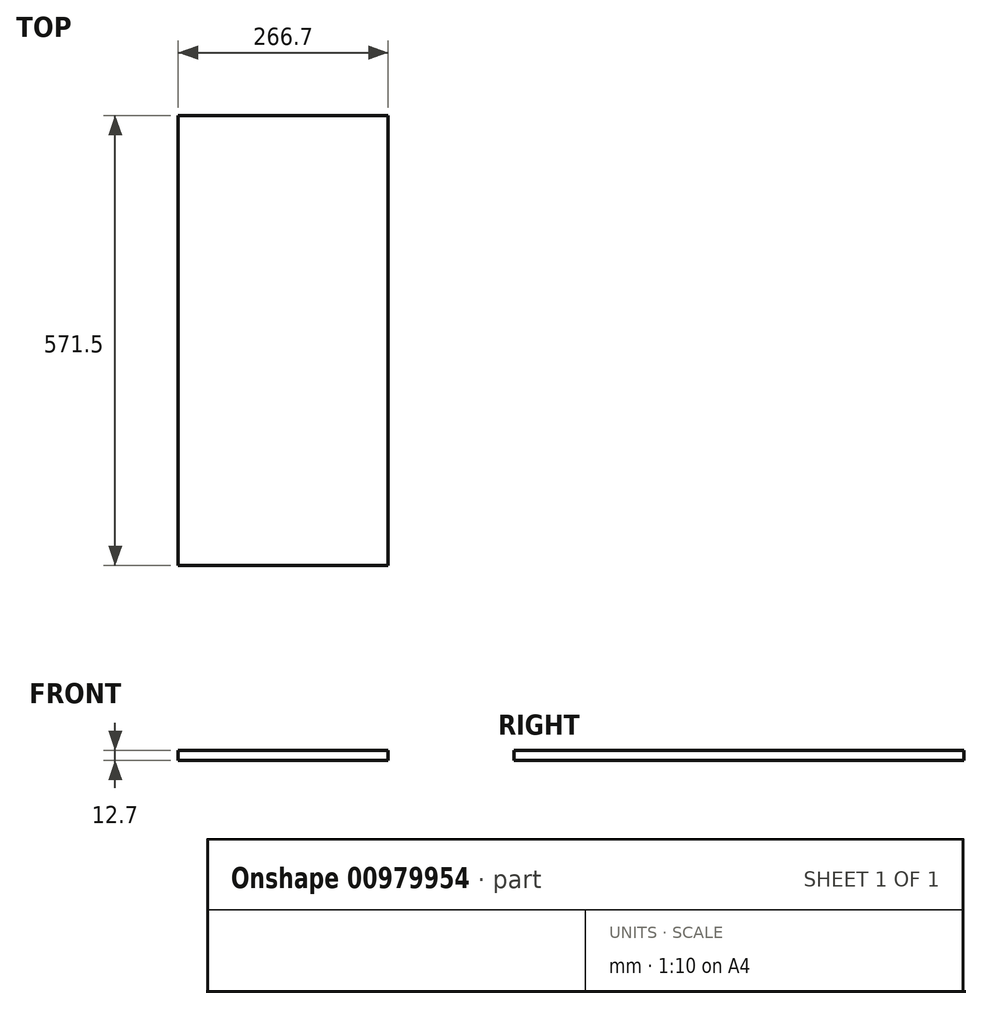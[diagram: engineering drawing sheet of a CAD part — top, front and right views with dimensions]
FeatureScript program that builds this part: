
annotation { "Feature Type Name" : "Feature", "Feature Type Description" : "" }
export const myFeature = defineFeature(function(context is Context, id is Id, definition is map)
    precondition{}
    {
        {
            var Q0;
            Q0=qCreatedBy(makeId("Top.planeOp"),FACE);
            var sketch = newSketch(context, id + "F0", { "sketchPlane" : qUnion([Q0])});
            skLineSegment(sketch, "E0.bottom", {"start": v(-133.35, 285.75) * mm, "end": v(133.35, 285.75) * mm});
            skLineSegment(sketch, "E0.top", {"start": v(-133.35, -285.75) * mm, "end": v(133.35, -285.75) * mm});
            skLineSegment(sketch, "E0.left", {"start": v(-133.35, 285.75) * mm, "end": v(-133.35, -285.75) * mm});
            skLineSegment(sketch, "E0.right", {"start": v(133.35, 285.75) * mm, "end": v(133.35, -285.75) * mm});
            skSolve(sketch);
        }
        {
            var Q0;
            Q0=qSketchRegion(id+"F0",true);
            extrude(context, id + "F1", {"entities" : qUnion([Q0]), "oppositeDirection" : true, "depth" : 12.7 * mm, "offsetDistance" : 25.4 * mm});
        }
    });
